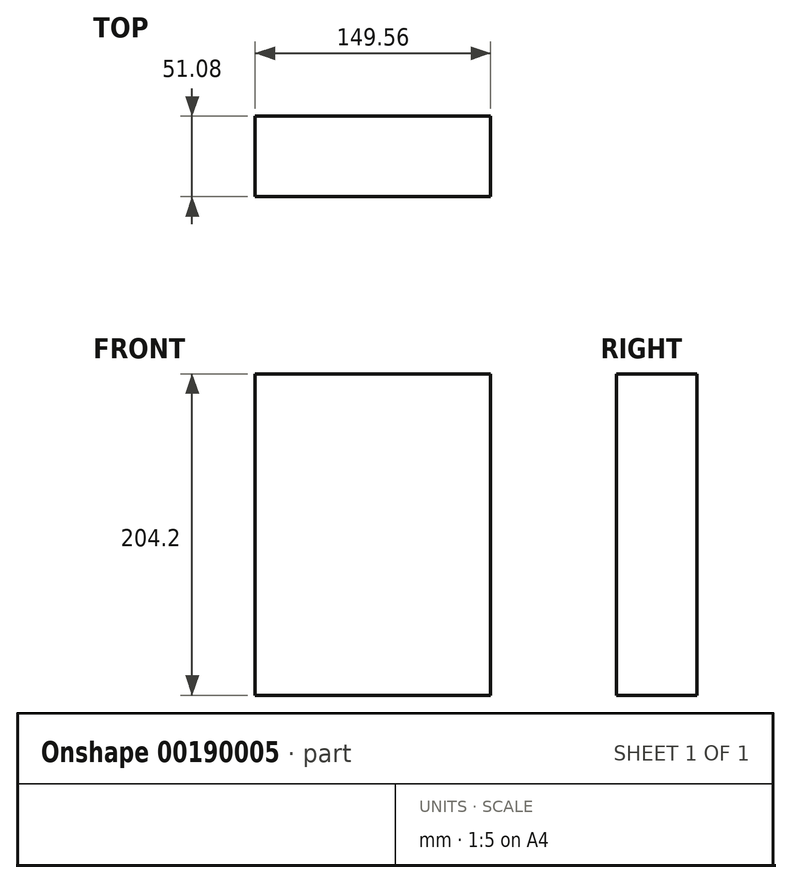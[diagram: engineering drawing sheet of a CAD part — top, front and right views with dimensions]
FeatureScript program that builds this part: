
annotation { "Feature Type Name" : "Feature", "Feature Type Description" : "" }
export const myFeature = defineFeature(function(context is Context, id is Id, definition is map)
    precondition{}
    {
        {
            var Q0;
            Q0=qCreatedBy(makeId("Front.planeOp"),FACE);
            var sketch = newSketch(context, id + "F0", { "sketchPlane" : qUnion([Q0])});
            skLineSegment(sketch, "E0.bottom", {"start": v(-84.86, -93.9) * mm, "end": v(64.7, -93.9) * mm});
            skLineSegment(sketch, "E0.top", {"start": v(-84.86, 110.3) * mm, "end": v(64.7, 110.3) * mm});
            skLineSegment(sketch, "E0.left", {"start": v(-84.86, -93.9) * mm, "end": v(-84.86, 110.3) * mm});
            skLineSegment(sketch, "E0.right", {"start": v(64.7, -93.9) * mm, "end": v(64.7, 110.3) * mm});
            skSolve(sketch);
        }
        {
            var Q0;
            Q0 = qSketchRegion(id + "F0", true);
            extrude(context, id + "F3", {"entities" : qUnion([Q0]), "depth" : 51.08 * mm});
        }
    });
